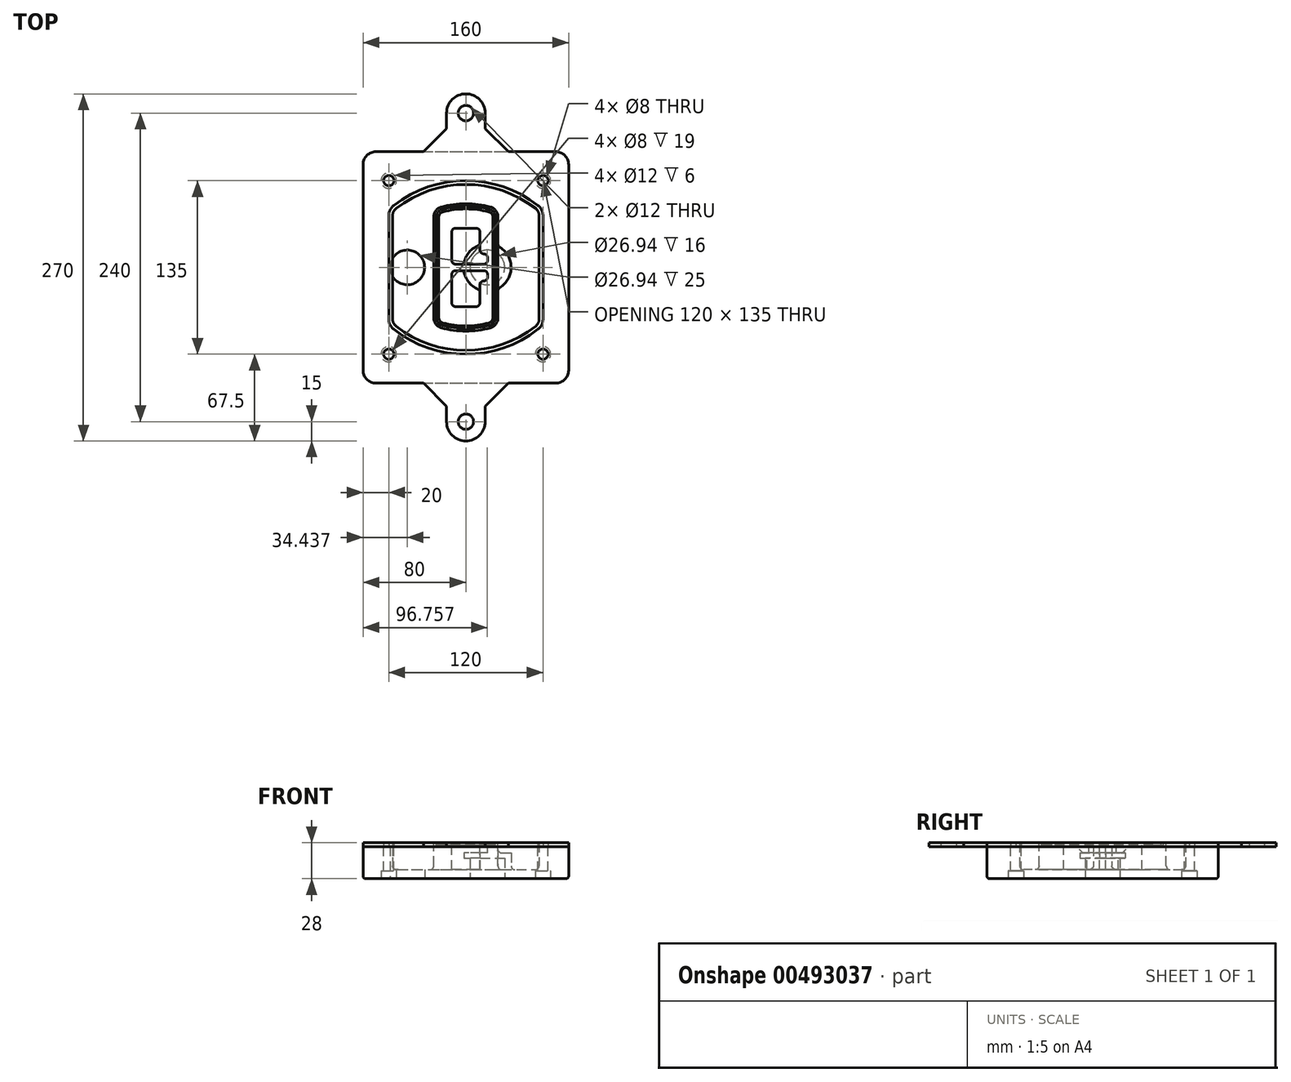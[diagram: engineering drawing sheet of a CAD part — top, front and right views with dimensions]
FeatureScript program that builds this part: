
annotation { "Feature Type Name" : "Feature", "Feature Type Description" : "" }
export const myFeature = defineFeature(function(context is Context, id is Id, definition is map)
    precondition{}
    {
        {
            var Q0;
            Q0=qCreatedBy(makeId("Top.planeOp"),FACE);
            var sketch = newSketch(context, id + "F0", { "sketchPlane" : qUnion([Q0])});
            skPoint(sketch, "E0.rect.middle", {"position": v(0, 0) * mm});
            skLineSegment(sketch, "E1.bottom", {"start": v(-70, -90) * mm, "end": v(70, -90) * mm});
            skLineSegment(sketch, "E1.top", {"start": v(-70, 90) * mm, "end": v(70, 90) * mm});
            skLineSegment(sketch, "E1.left", {"start": v(-80, -80) * mm, "end": v(-80, 80) * mm});
            skLineSegment(sketch, "E1.right", {"start": v(80, -80) * mm, "end": v(80, 80) * mm});
            skLineSegment(sketch, "E2", {"start": v(-80, 90) * mm, "end": v(80, -90) * mm, "construction": true});
            skLineSegment(sketch, "E3", {"start": v(80, 90) * mm, "end": v(-80, -90) * mm, "construction": true});
            skCircle(sketch, "E4", {"center": v(-60, 67.5) * mm, "radius": 4 * mm});
            skCircle(sketch, "E5", {"center": v(60, 67.5) * mm, "radius": 4 * mm});
            skCircle(sketch, "E6", {"center": v(60, -67.5) * mm, "radius": 4 * mm});
            skCircle(sketch, "E7", {"center": v(-60, -67.5) * mm, "radius": 4 * mm});
            skLineSegment(sketch, "E8", {"start": v(-60, 67.5) * mm, "end": v(60, 67.5) * mm, "construction": true});
            skLineSegment(sketch, "E9", {"start": v(60, 67.5) * mm, "end": v(60, -67.5) * mm, "construction": true});
            skLineSegment(sketch, "E10", {"start": v(60, -67.5) * mm, "end": v(-60, -67.5) * mm, "construction": true});
            skLineSegment(sketch, "E11", {"start": v(-60, -67.5) * mm, "end": v(-60, 67.5) * mm, "construction": true});
            skLineSegment(sketch, "E12", {"start": v(-60, 40.3) * mm, "end": v(-60, -40.3) * mm});
            skLineSegment(sketch, "E13", {"start": v(60, 40.3) * mm, "end": v(60, -40.3) * mm});
            skArc(sketch, "E14", {"start": v(56.15, 48.18) * mm, "mid": v(0, 67.5) * mm, "end": v(-56.15, 48.18) * mm});
            skArc(sketch, "E15", {"start": v(-56.15, -48.18) * mm, "mid": v(0, -67.5) * mm, "end": v(56.15, -48.18) * mm});
            skLineSegment(sketch, "E16", {"start": v(-60, 0) * mm, "end": v(60, 0) * mm, "construction": true});
            skPoint(sketch, "E17.visualSharp", {"position": v(-60, -45) * mm});
            skArc(sketch, "E17.filletArc", {"start": v(-60, -40.3) * mm, "mid": v(-58.99, -44.68) * mm, "end": v(-56.15, -48.18) * mm});
            skPoint(sketch, "E18.visualSharp", {"position": v(-60, 45) * mm});
            skArc(sketch, "E18.filletArc", {"start": v(-56.15, 48.18) * mm, "mid": v(-58.99, 44.68) * mm, "end": v(-60, 40.3) * mm});
            skPoint(sketch, "E19.visualSharp", {"position": v(60, 45) * mm});
            skArc(sketch, "E19.filletArc", {"start": v(60, 40.3) * mm, "mid": v(58.99, 44.68) * mm, "end": v(56.15, 48.18) * mm});
            skPoint(sketch, "E20.visualSharp", {"position": v(60, -45) * mm});
            skArc(sketch, "E20.filletArc", {"start": v(56.15, -48.18) * mm, "mid": v(58.99, -44.68) * mm, "end": v(60, -40.3) * mm});
            skPoint(sketch, "E21.visualSharp", {"position": v(-80, 90) * mm});
            skArc(sketch, "E21.filletArc", {"start": v(-70, 90) * mm, "mid": v(-77.07, 87.07) * mm, "end": v(-80, 80) * mm});
            skPoint(sketch, "E22.visualSharp", {"position": v(80, 90) * mm});
            skArc(sketch, "E22.filletArc", {"start": v(80, 80) * mm, "mid": v(77.07, 87.07) * mm, "end": v(70, 90) * mm});
            skPoint(sketch, "E23.visualSharp", {"position": v(80, -90) * mm});
            skArc(sketch, "E23.filletArc", {"start": v(70, -90) * mm, "mid": v(77.07, -87.07) * mm, "end": v(80, -80) * mm});
            skPoint(sketch, "E24.visualSharp", {"position": v(-80, -90) * mm});
            skArc(sketch, "E24.filletArc", {"start": v(-80, -80) * mm, "mid": v(-77.07, -87.07) * mm, "end": v(-70, -90) * mm});
            skArc(sketch, "E25.0", {"start": v(57, 40.3) * mm, "mid": v(56.3, 43.36) * mm, "end": v(54.3, 45.81) * mm});
            skLineSegment(sketch, "E25.1", {"start": v(57, 40.3) * mm, "end": v(57, -40.3) * mm});
            skArc(sketch, "E25.2", {"start": v(54.3, -45.81) * mm, "mid": v(56.3, -43.36) * mm, "end": v(57, -40.3) * mm});
            skArc(sketch, "E25.3", {"start": v(-54.3, -45.81) * mm, "mid": v(0, -64.5) * mm, "end": v(54.3, -45.81) * mm});
            skArc(sketch, "E25.4", {"start": v(-57, -40.3) * mm, "mid": v(-56.3, -43.36) * mm, "end": v(-54.3, -45.81) * mm});
            skArc(sketch, "E25.5", {"start": v(54.3, 45.81) * mm, "mid": v(0, 64.5) * mm, "end": v(-54.3, 45.81) * mm});
            skLineSegment(sketch, "E25.6", {"start": v(-57, 40.3) * mm, "end": v(-57, -40.3) * mm});
            skArc(sketch, "E25.7", {"start": v(-54.3, 45.81) * mm, "mid": v(-56.3, 43.36) * mm, "end": v(-57, 40.3) * mm});
            skArc(sketch, "E26.0", {"start": v(-58.62, 51.33) * mm, "mid": v(-62.58, 46.43) * mm, "end": v(-64, 40.3) * mm});
            skArc(sketch, "E26.1", {"start": v(58.62, 51.33) * mm, "mid": v(0, 71.5) * mm, "end": v(-58.62, 51.33) * mm});
            skArc(sketch, "E26.2", {"start": v(64, 40.3) * mm, "mid": v(62.58, 46.43) * mm, "end": v(58.62, 51.33) * mm});
            skLineSegment(sketch, "E26.3", {"start": v(64, 40.3) * mm, "end": v(64, -40.3) * mm});
            skArc(sketch, "E26.4", {"start": v(58.62, -51.33) * mm, "mid": v(62.58, -46.43) * mm, "end": v(64, -40.3) * mm});
            skLineSegment(sketch, "E26.5", {"start": v(-64, 40.3) * mm, "end": v(-64, -40.3) * mm});
            skArc(sketch, "E26.6", {"start": v(-58.62, -51.33) * mm, "mid": v(0, -71.5) * mm, "end": v(58.62, -51.33) * mm});
            skArc(sketch, "E26.7", {"start": v(-64, -40.3) * mm, "mid": v(-62.58, -46.43) * mm, "end": v(-58.62, -51.33) * mm});
            skSolve(sketch);
        }
        {
            var Q0;
            Q0=makeQuery(id+"F0.imprint","IMPRINT",FACE,{"disambiguationData":[TD([[makeQuery(id+"F0.imprint","IMPRINT",EDGE,{"derivedFrom":sQuery(id+"F0.wireOp",EDGE,"E1.bottom")}),1.0]])]});
            var Q1;
            Q1=makeQuery(id+"F0.imprint","IMPRINT",FACE,{"disambiguationData":[TD([[makeQuery(id+"F0.imprint","IMPRINT",EDGE,{"derivedFrom":sQuery(id+"F0.wireOp",EDGE,"E12")}),1.0]])]});
            var Q2;
            Q2=makeQuery(id+"F0.imprint","IMPRINT",FACE,{"disambiguationData":[TD([[makeQuery(id+"F0.imprint","IMPRINT",EDGE,{"derivedFrom":sQuery(id+"F0.wireOp",EDGE,"E25.0")}),1.0]])]});
            var Q3;
            Q3=makeQuery(id+"F0.imprint","IMPRINT",FACE,{"disambiguationData":[TD([[makeQuery(id+"F0.imprint","IMPRINT",EDGE,{"derivedFrom":sQuery(id+"F0.wireOp",EDGE,"E12")}),-1.0]])]});
            extrude(context, id + "F1", {"entities" : qUnion([Q0, Q1, Q2, Q3]), "oppositeDirection" : true, "depth" : 25 * mm});
        }
        {
            var Q0;
            Q0=makeQuery(id+"F0.imprint","IMPRINT",FACE,{"disambiguationData":[TD([[makeQuery(id+"F0.imprint","IMPRINT",EDGE,{"derivedFrom":sQuery(id+"F0.wireOp",EDGE,"E12")}),1.0]])]});
            extrude(context, id + "F2", {"entities" : qUnion([Q0]), "operationType" : NewBodyOperationType.ADD, "depth" : 3 * mm});
        }
        {
            var Q0;
            Q0=makeQuery(id+"F0.imprint","IMPRINT",FACE,{"disambiguationData":[TD([[makeQuery(id+"F0.imprint","IMPRINT",EDGE,{"derivedFrom":sQuery(id+"F0.wireOp",EDGE,"E25.0")}),1.0]])]});
            extrude(context, id + "F3", {"entities" : qUnion([Q0]), "operationType" : NewBodyOperationType.REMOVE, "oppositeDirection" : true, "depth" : 18 * mm});
        }
        {
            var Q0;
            Q0=makeQuery(id+"F2.opExtrude","CAP_FACE",FACE,{"disambiguationData":[OSD([sQuery(id+"F0.wireOp",EDGE,"E12"),sQuery(id+"F0.wireOp",EDGE,"E13"),sQuery(id+"F0.wireOp",EDGE,"E14"),sQuery(id+"F0.wireOp",EDGE,"E15"),sQuery(id+"F0.wireOp",EDGE,"E17.filletArc"),sQuery(id+"F0.wireOp",EDGE,"E18.filletArc"),sQuery(id+"F0.wireOp",EDGE,"E19.filletArc"),sQuery(id+"F0.wireOp",EDGE,"E20.filletArc"),sQuery(id+"F0.wireOp",EDGE,"E25.0"),sQuery(id+"F0.wireOp",EDGE,"E25.1"),sQuery(id+"F0.wireOp",EDGE,"E25.2"),sQuery(id+"F0.wireOp",EDGE,"E25.3"),sQuery(id+"F0.wireOp",EDGE,"E25.4"),sQuery(id+"F0.wireOp",EDGE,"E25.5"),sQuery(id+"F0.wireOp",EDGE,"E25.6"),sQuery(id+"F0.wireOp",EDGE,"E25.7")])],"isStart":false});
            var sketch = newSketch(context, id + "F4", { "sketchPlane" : qUnion([Q0])});
            skArc(sketch, "E27.0", {"start": v(-19.08, -46.97) * mm, "mid": v(0, -49.5) * mm, "end": v(19.08, -46.97) * mm});
            skArc(sketch, "E28.0", {"start": v(19.08, 46.97) * mm, "mid": v(0, 49.5) * mm, "end": v(-19.08, 46.97) * mm});
            skLineSegment(sketch, "E29", {"start": v(-25, 39.25) * mm, "end": v(-25, -39.25) * mm});
            skLineSegment(sketch, "E30", {"start": v(25, 39.25) * mm, "end": v(25, -39.25) * mm});
            skLineSegment(sketch, "E31", {"start": v(-25, 45.1) * mm, "end": v(25, 45.1) * mm, "construction": true});
            skLineSegment(sketch, "E32", {"start": v(-25, -45.1) * mm, "end": v(25, -45.1) * mm, "construction": true});
            skPoint(sketch, "E33.visualSharp", {"position": v(-25, 45.1) * mm});
            skArc(sketch, "E33.filletArc", {"start": v(-19.08, 46.97) * mm, "mid": v(-23.35, 44.11) * mm, "end": v(-25, 39.25) * mm});
            skPoint(sketch, "E34.visualSharp", {"position": v(25, 45.1) * mm});
            skArc(sketch, "E34.filletArc", {"start": v(25, 39.25) * mm, "mid": v(23.35, 44.11) * mm, "end": v(19.08, 46.97) * mm});
            skPoint(sketch, "E35.visualSharp", {"position": v(25, -45.1) * mm});
            skArc(sketch, "E35.filletArc", {"start": v(19.08, -46.97) * mm, "mid": v(23.35, -44.11) * mm, "end": v(25, -39.25) * mm});
            skPoint(sketch, "E36.visualSharp", {"position": v(-25, -45.1) * mm});
            skArc(sketch, "E36.filletArc", {"start": v(-25, -39.25) * mm, "mid": v(-23.35, -44.11) * mm, "end": v(-19.08, -46.97) * mm});
            skArc(sketch, "E37.0", {"start": v(54.3, 45.81) * mm, "mid": v(0, 64.5) * mm, "end": v(-54.3, 45.81) * mm});
            skArc(sketch, "E37.1", {"start": v(-54.3, 45.81) * mm, "mid": v(-56.3, 43.36) * mm, "end": v(-57, 40.3) * mm});
            skLineSegment(sketch, "E37.2", {"start": v(-57, 40.3) * mm, "end": v(-57, -40.3) * mm});
            skArc(sketch, "E37.3", {"start": v(-57, -40.3) * mm, "mid": v(-56.3, -43.36) * mm, "end": v(-54.3, -45.81) * mm});
            skArc(sketch, "E37.4", {"start": v(-54.3, -45.81) * mm, "mid": v(0, -64.5) * mm, "end": v(54.3, -45.81) * mm});
            skArc(sketch, "E37.5", {"start": v(54.3, -45.81) * mm, "mid": v(56.3, -43.36) * mm, "end": v(57, -40.3) * mm});
            skLineSegment(sketch, "E37.6", {"start": v(57, 40.3) * mm, "end": v(57, -40.3) * mm});
            skArc(sketch, "E37.7", {"start": v(57, 40.3) * mm, "mid": v(56.3, 43.36) * mm, "end": v(54.3, 45.81) * mm});
            skLineSegment(sketch, "E38.0", {"start": v(23, 39.25) * mm, "end": v(23, -39.25) * mm});
            skArc(sketch, "E38.1", {"start": v(18.56, -45.04) * mm, "mid": v(21.76, -42.9) * mm, "end": v(23, -39.25) * mm});
            skArc(sketch, "E38.2", {"start": v(-18.56, -45.04) * mm, "mid": v(0, -47.5) * mm, "end": v(18.56, -45.04) * mm});
            skArc(sketch, "E38.3", {"start": v(-23, -39.25) * mm, "mid": v(-21.76, -42.9) * mm, "end": v(-18.56, -45.04) * mm});
            skLineSegment(sketch, "E38.4", {"start": v(-23, 39.25) * mm, "end": v(-23, -39.25) * mm});
            skArc(sketch, "E38.5", {"start": v(23, 39.25) * mm, "mid": v(21.76, 42.9) * mm, "end": v(18.56, 45.04) * mm});
            skArc(sketch, "E38.6", {"start": v(-18.56, 45.04) * mm, "mid": v(-21.76, 42.9) * mm, "end": v(-23, 39.25) * mm});
            skArc(sketch, "E38.7", {"start": v(18.56, 45.04) * mm, "mid": v(0, 47.5) * mm, "end": v(-18.56, 45.04) * mm});
            skArc(sketch, "E39.0", {"start": v(21, 39.25) * mm, "mid": v(20.18, 41.68) * mm, "end": v(18.04, 43.1) * mm});
            skLineSegment(sketch, "E39.1", {"start": v(21, 39.25) * mm, "end": v(21, -39.25) * mm});
            skArc(sketch, "E39.2", {"start": v(18.04, -43.1) * mm, "mid": v(20.18, -41.68) * mm, "end": v(21, -39.25) * mm});
            skArc(sketch, "E39.3", {"start": v(-18.04, -43.1) * mm, "mid": v(0, -45.5) * mm, "end": v(18.04, -43.1) * mm});
            skArc(sketch, "E39.4", {"start": v(-21, -39.25) * mm, "mid": v(-20.18, -41.68) * mm, "end": v(-18.04, -43.1) * mm});
            skArc(sketch, "E39.5", {"start": v(18.04, 43.1) * mm, "mid": v(0, 45.5) * mm, "end": v(-18.04, 43.1) * mm});
            skLineSegment(sketch, "E39.6", {"start": v(-21, 39.25) * mm, "end": v(-21, -39.25) * mm});
            skArc(sketch, "E39.7", {"start": v(-18.04, 43.1) * mm, "mid": v(-20.18, 41.68) * mm, "end": v(-21, 39.25) * mm});
            skLineSegment(sketch, "E40", {"start": v(-25, 0) * mm, "end": v(25, 0) * mm, "construction": true});
            skLineSegment(sketch, "E41", {"start": v(-11, 5.5) * mm, "end": v(-11, 27.5) * mm});
            skLineSegment(sketch, "E42", {"start": v(-8, 30.5) * mm, "end": v(8, 30.5) * mm});
            skLineSegment(sketch, "E43", {"start": v(11, 27.5) * mm, "end": v(11, 13.5) * mm});
            skLineSegment(sketch, "E44", {"start": v(14, 10.5) * mm, "end": v(14, 10.5) * mm});
            skLineSegment(sketch, "E45", {"start": v(17, 7.5) * mm, "end": v(17, 5.5) * mm});
            skLineSegment(sketch, "E46", {"start": v(14, 2.5) * mm, "end": v(-8, 2.5) * mm});
            skPoint(sketch, "E47.visualSharp", {"position": v(-11, 30.5) * mm});
            skArc(sketch, "E47.filletArc", {"start": v(-8, 30.5) * mm, "mid": v(-10.12, 29.62) * mm, "end": v(-11, 27.5) * mm});
            skPoint(sketch, "E48.visualSharp", {"position": v(11, 30.5) * mm});
            skArc(sketch, "E48.filletArc", {"start": v(11, 27.5) * mm, "mid": v(10.12, 29.62) * mm, "end": v(8, 30.5) * mm});
            skPoint(sketch, "E49.visualSharp", {"position": v(11, 10.5) * mm});
            skArc(sketch, "E49.filletArc", {"start": v(11, 13.5) * mm, "mid": v(11.88, 11.38) * mm, "end": v(14, 10.5) * mm});
            skPoint(sketch, "E50.visualSharp", {"position": v(17, 10.5) * mm});
            skArc(sketch, "E50.filletArc", {"start": v(17, 7.5) * mm, "mid": v(16.12, 9.62) * mm, "end": v(14, 10.5) * mm});
            skPoint(sketch, "E51.visualSharp", {"position": v(17, 2.5) * mm});
            skArc(sketch, "E51.filletArc", {"start": v(14, 2.5) * mm, "mid": v(16.12, 3.38) * mm, "end": v(17, 5.5) * mm});
            skPoint(sketch, "E52.visualSharp", {"position": v(-11, 2.5) * mm});
            skArc(sketch, "E52.filletArc", {"start": v(-11, 5.5) * mm, "mid": v(-10.12, 3.38) * mm, "end": v(-8, 2.5) * mm});
            skLineSegment(sketch, "E53.0.MirrorCS", {"start": v(14, -2.5) * mm, "end": v(-8, -2.5) * mm});
            skArc(sketch, "E54.0.MirrorCS", {"start": v(-11, -5.5) * mm, "mid": v(-10.12, -3.38) * mm, "end": v(-8, -2.5) * mm});
            skLineSegment(sketch, "E55.0.MirrorCS", {"start": v(-11, -5.5) * mm, "end": v(-11, -27.5) * mm});
            skArc(sketch, "E56.0.MirrorCS", {"start": v(-8, -30.5) * mm, "mid": v(-10.12, -29.62) * mm, "end": v(-11, -27.5) * mm});
            skLineSegment(sketch, "E57.0.MirrorCS", {"start": v(-8, -30.5) * mm, "end": v(8, -30.5) * mm});
            skArc(sketch, "E58.0.MirrorCS", {"start": v(11, -27.5) * mm, "mid": v(10.12, -29.62) * mm, "end": v(8, -30.5) * mm});
            skLineSegment(sketch, "E59.0.MirrorCS", {"start": v(11, -27.5) * mm, "end": v(11, -13.5) * mm});
            skArc(sketch, "E60.0.MirrorCS", {"start": v(11, -13.5) * mm, "mid": v(11.88, -11.38) * mm, "end": v(14, -10.5) * mm});
            skArc(sketch, "E61.0.MirrorCS", {"start": v(17, -7.5) * mm, "mid": v(16.12, -9.62) * mm, "end": v(14, -10.5) * mm});
            skLineSegment(sketch, "E62.0.MirrorCS", {"start": v(17, -7.5) * mm, "end": v(17, -5.5) * mm});
            skArc(sketch, "E63.0.MirrorCS", {"start": v(14, -2.5) * mm, "mid": v(16.12, -3.38) * mm, "end": v(17, -5.5) * mm});
            skSolve(sketch);
        }
        {
            var Q0;
            Q0=makeQuery(id+"F4.imprint","IMPRINT",FACE,{"disambiguationData":[TD([[makeQuery(id+"F4.imprint","IMPRINT",EDGE,{"derivedFrom":sQuery(id+"F4.wireOp",EDGE,"E27.0")}),1.0]])]});
            var Q1;
            Q1=makeQuery(id+"F4.imprint","IMPRINT",FACE,{"disambiguationData":[TD([[makeQuery(id+"F4.imprint","IMPRINT",EDGE,{"derivedFrom":sQuery(id+"F4.wireOp",EDGE,"E38.0")}),-1.0]])]});
            var Q2;
            Q2=makeQuery(id+"F4.imprint","IMPRINT",FACE,{"disambiguationData":[TD([[makeQuery(id+"F4.imprint","IMPRINT",EDGE,{"derivedFrom":sQuery(id+"F4.wireOp",EDGE,"E39.0")}),1.0]])]});
            extrude(context, id + "F5", {"entities" : qUnion([Q0, Q1, Q2]), "operationType" : NewBodyOperationType.ADD, "endBound" : BoundingType.UP_TO_NEXT, "oppositeDirection" : true, "depth" : 25 * mm});
        }
        {
            var Q0;
            Q0=makeQuery(id+"F4.imprint","IMPRINT",FACE,{"disambiguationData":[TD([[makeQuery(id+"F4.imprint","IMPRINT",EDGE,{"derivedFrom":sQuery(id+"F4.wireOp",EDGE,"E38.0")}),-1.0]])]});
            extrude(context, id + "F6", {"entities" : qUnion([Q0]), "operationType" : NewBodyOperationType.REMOVE, "oppositeDirection" : true, "depth" : 2 * mm});
        }
        {
            var Q0;
            Q0=makeQuery(id+"F1.opExtrude","CAP_FACE",FACE,{"disambiguationData":[OSD([sQuery(id+"F0.wireOp",EDGE,"E1.bottom"),sQuery(id+"F0.wireOp",EDGE,"E1.top"),sQuery(id+"F0.wireOp",EDGE,"E1.left"),sQuery(id+"F0.wireOp",EDGE,"E1.right"),sQuery(id+"F0.wireOp",EDGE,"E4"),sQuery(id+"F0.wireOp",EDGE,"E5"),sQuery(id+"F0.wireOp",EDGE,"E6"),sQuery(id+"F0.wireOp",EDGE,"E7"),sQuery(id+"F0.wireOp",EDGE,"E21.filletArc"),sQuery(id+"F0.wireOp",EDGE,"E22.filletArc"),sQuery(id+"F0.wireOp",EDGE,"E23.filletArc"),sQuery(id+"F0.wireOp",EDGE,"E24.filletArc")])],"isStart":false});
            var sketch = newSketch(context, id + "F7", { "sketchPlane" : qUnion([Q0])});
            skCircle(sketch, "E64", {"center": v(16.76, 0) * mm, "radius": 13.47 * mm});
            skCircle(sketch, "E65", {"center": v(-45.56, 0) * mm, "radius": 13.47 * mm});
            skLineSegment(sketch, "E66", {"start": v(80, 0) * mm, "end": v(-80, 0) * mm});
            skCircle(sketch, "E67", {"center": v(16.76, 0) * mm, "radius": 18.47 * mm});
            skCircle(sketch, "E68", {"center": v(60, -67.5) * mm, "radius": 6 * mm});
            skCircle(sketch, "E69", {"center": v(-60, -67.5) * mm, "radius": 6 * mm});
            skCircle(sketch, "E70", {"center": v(-60, 67.5) * mm, "radius": 6 * mm});
            skCircle(sketch, "E71", {"center": v(60, 67.5) * mm, "radius": 6 * mm});
            skSolve(sketch);
        }
        {
            var Q0;
            {var subQ1=sQuery(id+"F7.wireOp",EDGE,"E66");var subQ4=sQuery(id+"F7.wireOp",EDGE,"E64");var subQ6=makeQuery(id+"F7.imprint","INTERSECT",VERTEX,{"disambiguationData":[OD(0.0)],"derivedFrom":[subQ4,subQ1]});Q0=makeQuery(id+"F7.imprint","IMPRINT",FACE,{"disambiguationData":[TD([[makeQuery(id+"F7.imprint","IMPRINT",EDGE,{"disambiguationData":[TD([[subQ6,-1.0]])],"derivedFrom":subQ4}),-1.0]])]});}
            var Q1;
            {var subQ0=sQuery(id+"F7.wireOp",EDGE,"E66");var subQ1=sQuery(id+"F7.wireOp",EDGE,"E64");var subQ3=makeQuery(id+"F7.imprint","INTERSECT",VERTEX,{"disambiguationData":[OD(0.0)],"derivedFrom":[subQ1,subQ0]});Q1=makeQuery(id+"F7.imprint","IMPRINT",FACE,{"disambiguationData":[TD([[makeQuery(id+"F7.imprint","IMPRINT",EDGE,{"disambiguationData":[TD([[subQ3,-1.0]])],"derivedFrom":subQ1}),1.0]])]});}
            var Q2;
            {var subQ0=sQuery(id+"F7.wireOp",EDGE,"E66");var subQ1=sQuery(id+"F7.wireOp",EDGE,"E64");var subQ3=makeQuery(id+"F7.imprint","INTERSECT",VERTEX,{"disambiguationData":[OD(0.0)],"derivedFrom":[subQ1,subQ0]});Q2=makeQuery(id+"F7.imprint","IMPRINT",FACE,{"disambiguationData":[TD([[makeQuery(id+"F7.imprint","IMPRINT",EDGE,{"disambiguationData":[TD([[subQ3,1.0]])],"derivedFrom":subQ1}),1.0]])]});}
            var Q3;
            {var subQ1=sQuery(id+"F7.wireOp",EDGE,"E66");var subQ4=sQuery(id+"F7.wireOp",EDGE,"E64");var subQ6=makeQuery(id+"F7.imprint","INTERSECT",VERTEX,{"disambiguationData":[OD(0.0)],"derivedFrom":[subQ4,subQ1]});Q3=makeQuery(id+"F7.imprint","IMPRINT",FACE,{"disambiguationData":[TD([[makeQuery(id+"F7.imprint","IMPRINT",EDGE,{"disambiguationData":[TD([[subQ6,1.0]])],"derivedFrom":subQ4}),-1.0]])]});}
            extrude(context, id + "F8", {"entities" : qUnion([Q0, Q1, Q2, Q3]), "operationType" : NewBodyOperationType.ADD, "oppositeDirection" : true, "depth" : 20 * mm});
        }
        {
            var Q0;
            {var subQ0=sQuery(id+"F7.wireOp",EDGE,"E66");var subQ1=sQuery(id+"F7.wireOp",EDGE,"E64");var subQ3=makeQuery(id+"F7.imprint","INTERSECT",VERTEX,{"disambiguationData":[OD(0.0)],"derivedFrom":[subQ1,subQ0]});Q0=makeQuery(id+"F7.imprint","IMPRINT",FACE,{"disambiguationData":[TD([[makeQuery(id+"F7.imprint","IMPRINT",EDGE,{"disambiguationData":[TD([[subQ3,-1.0]])],"derivedFrom":subQ1}),1.0]])]});}
            var Q1;
            {var subQ0=sQuery(id+"F7.wireOp",EDGE,"E66");var subQ1=sQuery(id+"F7.wireOp",EDGE,"E64");var subQ3=makeQuery(id+"F7.imprint","INTERSECT",VERTEX,{"disambiguationData":[OD(0.0)],"derivedFrom":[subQ1,subQ0]});Q1=makeQuery(id+"F7.imprint","IMPRINT",FACE,{"disambiguationData":[TD([[makeQuery(id+"F7.imprint","IMPRINT",EDGE,{"disambiguationData":[TD([[subQ3,1.0]])],"derivedFrom":subQ1}),1.0]])]});}
            extrude(context, id + "F9", {"entities" : qUnion([Q0, Q1]), "operationType" : NewBodyOperationType.REMOVE, "oppositeDirection" : true, "depth" : 16 * mm});
        }
        {
            var Q0;
            {var subQ0=sQuery(id+"F7.wireOp",EDGE,"E66");var subQ1=sQuery(id+"F7.wireOp",EDGE,"E65");var subQ3=makeQuery(id+"F7.imprint","INTERSECT",VERTEX,{"disambiguationData":[OD(0.0)],"derivedFrom":[subQ1,subQ0]});Q0=makeQuery(id+"F7.imprint","IMPRINT",FACE,{"disambiguationData":[TD([[makeQuery(id+"F7.imprint","IMPRINT",EDGE,{"disambiguationData":[TD([[subQ3,-1.0]])],"derivedFrom":subQ1}),1.0]])]});}
            var Q1;
            {var subQ0=sQuery(id+"F7.wireOp",EDGE,"E66");var subQ1=sQuery(id+"F7.wireOp",EDGE,"E65");var subQ3=makeQuery(id+"F7.imprint","INTERSECT",VERTEX,{"disambiguationData":[OD(0.0)],"derivedFrom":[subQ1,subQ0]});Q1=makeQuery(id+"F7.imprint","IMPRINT",FACE,{"disambiguationData":[TD([[makeQuery(id+"F7.imprint","IMPRINT",EDGE,{"disambiguationData":[TD([[subQ3,1.0]])],"derivedFrom":subQ1}),1.0]])]});}
            extrude(context, id + "F10", {"entities" : qUnion([Q0, Q1]), "operationType" : NewBodyOperationType.REMOVE, "oppositeDirection" : true, "depth" : 25 * mm});
        }
        {
            var Q0;
            Q0=makeQuery(id+"F7.imprint","IMPRINT",FACE,{"disambiguationData":[TD([[makeQuery(id+"F7.imprint","IMPRINT",EDGE,{"derivedFrom":sQuery(id+"F7.wireOp",EDGE,"E68")}),1.0]])]});
            var Q1;
            Q1=makeQuery(id+"F7.imprint","IMPRINT",FACE,{"disambiguationData":[TD([[makeQuery(id+"F7.imprint","IMPRINT",EDGE,{"derivedFrom":makeQuery(id+"F1.opExtrude","CAP_EDGE",EDGE,{"disambiguationData":[OSD([sQuery(id+"F0.wireOp",EDGE,"E5")])],"isStart":false})}),-1.0]])]});
            var Q2;
            Q2=makeQuery(id+"F7.imprint","IMPRINT",FACE,{"disambiguationData":[TD([[makeQuery(id+"F7.imprint","IMPRINT",EDGE,{"derivedFrom":sQuery(id+"F7.wireOp",EDGE,"E69")}),1.0]])]});
            var Q3;
            Q3=makeQuery(id+"F7.imprint","IMPRINT",FACE,{"disambiguationData":[TD([[makeQuery(id+"F7.imprint","IMPRINT",EDGE,{"derivedFrom":makeQuery(id+"F1.opExtrude","CAP_EDGE",EDGE,{"disambiguationData":[OSD([sQuery(id+"F0.wireOp",EDGE,"E4")])],"isStart":false})}),-1.0]])]});
            var Q4;
            Q4=makeQuery(id+"F7.imprint","IMPRINT",FACE,{"disambiguationData":[TD([[makeQuery(id+"F7.imprint","IMPRINT",EDGE,{"derivedFrom":sQuery(id+"F7.wireOp",EDGE,"E70")}),1.0]])]});
            var Q5;
            Q5=makeQuery(id+"F7.imprint","IMPRINT",FACE,{"disambiguationData":[TD([[makeQuery(id+"F7.imprint","IMPRINT",EDGE,{"derivedFrom":makeQuery(id+"F1.opExtrude","CAP_EDGE",EDGE,{"disambiguationData":[OSD([sQuery(id+"F0.wireOp",EDGE,"E7")])],"isStart":false})}),-1.0]])]});
            var Q6;
            Q6=makeQuery(id+"F7.imprint","IMPRINT",FACE,{"disambiguationData":[TD([[makeQuery(id+"F7.imprint","IMPRINT",EDGE,{"derivedFrom":sQuery(id+"F7.wireOp",EDGE,"E71")}),1.0]])]});
            var Q7;
            Q7=makeQuery(id+"F7.imprint","IMPRINT",FACE,{"disambiguationData":[TD([[makeQuery(id+"F7.imprint","IMPRINT",EDGE,{"derivedFrom":makeQuery(id+"F1.opExtrude","CAP_EDGE",EDGE,{"disambiguationData":[OSD([sQuery(id+"F0.wireOp",EDGE,"E6")])],"isStart":false})}),-1.0]])]});
            extrude(context, id + "F11", {"entities" : qUnion([Q0, Q1, Q2, Q3, Q4, Q5, Q6, Q7]), "operationType" : NewBodyOperationType.REMOVE, "oppositeDirection" : true, "depth" : 6 * mm});
        }
        {
            var Q0;
            Q0=makeQuery(id+"F9.boolean.opBoolean","COPY",FACE,{"derivedFrom":makeQuery(id+"F9.opExtrude","CAP_FACE",FACE,{"disambiguationData":[OSD([sQuery(id+"F7.wireOp",EDGE,"E64")])],"isStart":false})});
            var sketch = newSketch(context, id + "F12", { "sketchPlane" : qUnion([Q0])});
            skArc(sketch, "E72.0", {"start": v(11, 17.55) * mm, "mid": v(2.57, 11.82) * mm, "end": v(-1.54, 2.5) * mm});
            skArc(sketch, "E72.1", {"start": v(-1.54, -2.5) * mm, "mid": v(2.57, -11.82) * mm, "end": v(11, -17.55) * mm});
            skLineSegment(sketch, "E73", {"start": v(-1.54, -2.5) * mm, "end": v(14, -2.5) * mm});
            skLineSegment(sketch, "E74.0", {"start": v(14, 2.5) * mm, "end": v(-1.54, 2.5) * mm});
            skArc(sketch, "E74.1", {"start": v(14, 2.5) * mm, "mid": v(16.12, 3.38) * mm, "end": v(17, 5.5) * mm});
            skLineSegment(sketch, "E74.2", {"start": v(17, 7.5) * mm, "end": v(17, 5.5) * mm});
            skArc(sketch, "E74.3", {"start": v(17, 7.5) * mm, "mid": v(16.12, 9.62) * mm, "end": v(14, 10.5) * mm});
            skArc(sketch, "E74.4", {"start": v(11, 13.5) * mm, "mid": v(11.88, 11.38) * mm, "end": v(14, 10.5) * mm});
            skLineSegment(sketch, "E74.5", {"start": v(11, 17.55) * mm, "end": v(11, 13.5) * mm});
            skLineSegment(sketch, "E74.7", {"start": v(14, -2.5) * mm, "end": v(-1.54, -2.5) * mm});
            skArc(sketch, "E74.8", {"start": v(14, -2.5) * mm, "mid": v(16.12, -3.38) * mm, "end": v(17, -5.5) * mm});
            skLineSegment(sketch, "E74.9", {"start": v(17, -7.5) * mm, "end": v(17, -5.5) * mm});
            skArc(sketch, "E74.10", {"start": v(17, -7.5) * mm, "mid": v(16.12, -9.62) * mm, "end": v(14, -10.5) * mm});
            skArc(sketch, "E74.11", {"start": v(11, -13.5) * mm, "mid": v(11.88, -11.38) * mm, "end": v(14, -10.5) * mm});
            skLineSegment(sketch, "E74.12", {"start": v(11, -17.55) * mm, "end": v(11, -13.5) * mm});
            skPoint(sketch, "E75.orphan", {"position": v(11, -27.5) * mm});
            skPoint(sketch, "E76.orphan", {"position": v(-8, -2.5) * mm});
            skPoint(sketch, "E77.orphan", {"position": v(-8, 2.5) * mm});
            skPoint(sketch, "E78.orphan", {"position": v(11, 27.5) * mm});
            skSolve(sketch);
        }
        {
            var Q0;
            {var subQ7=sQuery(id+"F12.wireOp",EDGE,"E72.0");var subQ14=sQuery(id+"F12.wireOp",EDGE,"E72.1");var subQ16=sQuery(id+"F12.wireOp",EDGE,"E74.1");var subQ18=sQuery(id+"F12.wireOp",EDGE,"E74.8");Q0=qUnion([makeQuery(id+"F12.imprint","IMPRINT",FACE,{"disambiguationData":[TD([[makeQuery(id+"F12.imprint","IMPRINT",EDGE,{"derivedFrom":subQ7}),1.0]])]}),makeQuery(id+"F12.imprint","IMPRINT",FACE,{"disambiguationData":[TD([[makeQuery(id+"F12.imprint","IMPRINT",EDGE,{"derivedFrom":subQ14}),1.0]])]}),makeQuery(id+"F12.imprint","IMPRINT",FACE,{"disambiguationData":[TD([[makeQuery(id+"F12.imprint","IMPRINT",EDGE,{"derivedFrom":subQ16}),1.0]])]}),makeQuery(id+"F12.imprint","IMPRINT",FACE,{"disambiguationData":[TD([[makeQuery(id+"F12.imprint","IMPRINT",EDGE,{"derivedFrom":subQ18}),-1.0]])]})]);}
            var Q1;
            Q1=makeQuery(id+"F5.boolean.opBoolean","SPLIT",FACE,{"disambiguationData":[TD([makeQuery(id+"F5.opExtrude","SWEPT_FACE",FACE,{"disambiguationData":[OSD([sQuery(id+"F4.wireOp",EDGE,"E41")])]})])],"derivedFrom":makeQuery(id+"F3.boolean.opBoolean","COPY",FACE,{"derivedFrom":makeQuery(id+"F3.opExtrude","CAP_FACE",FACE,{"disambiguationData":[OSD([sQuery(id+"F0.wireOp",EDGE,"E25.0"),sQuery(id+"F0.wireOp",EDGE,"E25.1"),sQuery(id+"F0.wireOp",EDGE,"E25.2"),sQuery(id+"F0.wireOp",EDGE,"E25.3"),sQuery(id+"F0.wireOp",EDGE,"E25.4"),sQuery(id+"F0.wireOp",EDGE,"E25.5"),sQuery(id+"F0.wireOp",EDGE,"E25.6"),sQuery(id+"F0.wireOp",EDGE,"E25.7")])],"isStart":false})})});
            extrude(context, id + "F13", {"entities" : qUnion([Q0]), "operationType" : NewBodyOperationType.REMOVE, "endBound" : BoundingType.UP_TO_SURFACE, "endBoundEntityFace" : qUnion([Q1]), "depth" : 25 * mm});
        }
        {
            var Q0;
            Q0=makeQuery(id+"F3.boolean.opBoolean","COPY",EDGE,{"derivedFrom":makeQuery(id+"F3.opExtrude","CAP_EDGE",EDGE,{"disambiguationData":[OSD([sQuery(id+"F0.wireOp",EDGE,"E25.6")])],"isStart":false})});
            var Q1;
            Q1=makeQuery(id+"F8.boolean.opBoolean","INTERSECT",EDGE,{"derivedFrom":[makeQuery(id+"F5.opExtrude","SWEPT_FACE",FACE,{"disambiguationData":[OSD([sQuery(id+"F4.wireOp",EDGE,"E30")])]}),makeQuery(id+"F8.opExtrude","CAP_FACE",FACE,{"disambiguationData":[OSD([sQuery(id+"F7.wireOp",EDGE,"E67")])],"isStart":false})]});
            var Q2;
            Q2=makeQuery(id+"F8.boolean.opBoolean","INTERSECT",EDGE,{"disambiguationData":[OD(1.0)],"derivedFrom":[makeQuery(id+"F5.opExtrude","SWEPT_FACE",FACE,{"disambiguationData":[OSD([sQuery(id+"F4.wireOp",EDGE,"E30")])]}),makeQuery(id+"F8.opExtrude","SWEPT_FACE",FACE,{"disambiguationData":[OSD([sQuery(id+"F7.wireOp",EDGE,"E67")])]})]});
            var Q3;
            {var subQ0=sQuery(id+"F4.wireOp",EDGE,"E30");Q3=makeQuery(id+"F8.boolean.opBoolean","SPLIT",EDGE,{"disambiguationData":[TD([makeQuery(id+"F5.opExtrude","SWEPT_FACE",FACE,{"disambiguationData":[OSD([sQuery(id+"F4.wireOp",EDGE,"E35.filletArc")])]})])],"derivedFrom":makeQuery(id+"F5.opExtrude","CAP_EDGE",EDGE,{"disambiguationData":[OSD([subQ0])],"isStart":false})});}
            var Q4;
            {var subQ0=sQuery(id+"F0.wireOp",EDGE,"E25.7");var subQ1=sQuery(id+"F0.wireOp",EDGE,"E25.1");var subQ2=sQuery(id+"F0.wireOp",EDGE,"E25.6");var subQ3=sQuery(id+"F0.wireOp",EDGE,"E25.5");var subQ4=sQuery(id+"F0.wireOp",EDGE,"E25.4");var subQ5=sQuery(id+"F0.wireOp",EDGE,"E25.0");var subQ6=sQuery(id+"F0.wireOp",EDGE,"E25.2");var subQ7=sQuery(id+"F0.wireOp",EDGE,"E25.3");Q4=makeQuery(id+"F8.boolean.opBoolean","INTERSECT",EDGE,{"derivedFrom":[makeQuery(id+"F5.boolean.opBoolean","SPLIT",FACE,{"disambiguationData":[TD([makeQuery(id+"F2.opExtrude","SWEPT_FACE",FACE,{"disambiguationData":[OSD([subQ5])]})])],"derivedFrom":makeQuery(id+"F3.boolean.opBoolean","COPY",FACE,{"derivedFrom":makeQuery(id+"F3.opExtrude","CAP_FACE",FACE,{"disambiguationData":[OSD([subQ5,subQ1,subQ6,subQ7,subQ4,subQ3,subQ2,subQ0])],"isStart":false})})}),makeQuery(id+"F8.opExtrude","SWEPT_FACE",FACE,{"disambiguationData":[OSD([sQuery(id+"F7.wireOp",EDGE,"E67")])]})]});}
            var Q5;
            Q5=makeQuery(id+"F8.boolean.opBoolean","INTERSECT",EDGE,{"disambiguationData":[OD(0.0)],"derivedFrom":[makeQuery(id+"F5.opExtrude","SWEPT_FACE",FACE,{"disambiguationData":[OSD([sQuery(id+"F4.wireOp",EDGE,"E30")])]}),makeQuery(id+"F8.opExtrude","SWEPT_FACE",FACE,{"disambiguationData":[OSD([sQuery(id+"F7.wireOp",EDGE,"E67")])]})]});
            fillet(context, id + "F14", {"entities" : qUnion([Q0, Q1, Q2, Q3, Q4, Q5]), "radius" : 3 * mm, "tangentPropagation" : true, "allowEdgeOverflow" : false});
        }
        {
            var Q0;
            Q0=makeQuery(id+"F1.opExtrude","CAP_EDGE",EDGE,{"disambiguationData":[OSD([sQuery(id+"F0.wireOp",EDGE,"E1.bottom")])],"isStart":false});
            fillet(context, id + "F15", {"entities" : qUnion([Q0]), "radius" : 2 * mm, "tangentPropagation" : true, "allowEdgeOverflow" : false});
        }
        {
            var Q0;
            {var subQ0=sQuery(id+"F0.wireOp",EDGE,"E21.filletArc");var subQ1=sQuery(id+"F0.wireOp",EDGE,"E7");var subQ2=sQuery(id+"F0.wireOp",EDGE,"E6");var subQ3=sQuery(id+"F0.wireOp",EDGE,"E5");var subQ4=sQuery(id+"F0.wireOp",EDGE,"E4");var subQ5=sQuery(id+"F0.wireOp",EDGE,"E22.filletArc");var subQ6=sQuery(id+"F0.wireOp",EDGE,"E1.bottom");var subQ7=sQuery(id+"F0.wireOp",EDGE,"E1.right");var subQ8=sQuery(id+"F0.wireOp",EDGE,"E1.top");var subQ9=sQuery(id+"F0.wireOp",EDGE,"E1.left");var subQ10=sQuery(id+"F0.wireOp",EDGE,"E23.filletArc");var subQ11=sQuery(id+"F0.wireOp",EDGE,"E24.filletArc");Q0=makeQuery(id+"F2.boolean.opBoolean","SPLIT",FACE,{"disambiguationData":[TD([makeQuery(id+"F1.opExtrude","SWEPT_FACE",FACE,{"disambiguationData":[OSD([subQ6])]})])],"derivedFrom":makeQuery(id+"F1.opExtrude","CAP_FACE",FACE,{"disambiguationData":[OSD([subQ6,subQ8,subQ9,subQ7,subQ4,subQ3,subQ2,subQ1,subQ0,subQ5,subQ10,subQ11])],"isStart":true})});}
            var sketch = newSketch(context, id + "F16", { "sketchPlane" : qUnion([Q0])});
            skLineSegment(sketch, "E79", {"start": v(0, 90) * mm, "end": v(0, 120) * mm, "construction": true});
            skCircle(sketch, "E80", {"center": v(0, 120) * mm, "radius": 6 * mm});
            skLineSegment(sketch, "E81", {"start": v(15, 120) * mm, "end": v(15, 108) * mm});
            skLineSegment(sketch, "E82", {"start": v(15, 108) * mm, "end": v(33, 90) * mm});
            skLineSegment(sketch, "E83", {"start": v(0, 90) * mm, "end": v(33, 90) * mm});
            skLineSegment(sketch, "E84.MirrorCS", {"start": v(0, 90) * mm, "end": v(-33, 90) * mm});
            skLineSegment(sketch, "E85.MirrorCS", {"start": v(-15, 120) * mm, "end": v(-15, 108) * mm});
            skLineSegment(sketch, "E86.MirrorCS", {"start": v(-15, 108) * mm, "end": v(-33, 90) * mm});
            skArc(sketch, "E87", {"start": v(-15, 120) * mm, "mid": v(0, 135) * mm, "end": v(15, 120) * mm});
            skLineSegment(sketch, "E88", {"start": v(-80, 0) * mm, "end": v(80, 0) * mm, "construction": true});
            skLineSegment(sketch, "E89.0", {"start": v(-70, 90) * mm, "end": v(70, 90) * mm});
            skArc(sketch, "E90.0", {"start": v(-70, 90) * mm, "mid": v(-77.07, 87.07) * mm, "end": v(-80, 80) * mm});
            skLineSegment(sketch, "E91.0", {"start": v(-80, -80) * mm, "end": v(-80, 80) * mm});
            skArc(sketch, "E92.0", {"start": v(-80, -80) * mm, "mid": v(-77.07, -87.07) * mm, "end": v(-70, -90) * mm});
            skLineSegment(sketch, "E93.0", {"start": v(-70, -90) * mm, "end": v(70, -90) * mm});
            skArc(sketch, "E94.0", {"start": v(70, -90) * mm, "mid": v(77.07, -87.07) * mm, "end": v(80, -80) * mm});
            skLineSegment(sketch, "E95.0", {"start": v(80, -80) * mm, "end": v(80, 80) * mm});
            skArc(sketch, "E96.0", {"start": v(80, 80) * mm, "mid": v(77.07, 87.07) * mm, "end": v(70, 90) * mm});
            skArc(sketch, "E97.0", {"start": v(56.15, 48.18) * mm, "mid": v(0, 67.5) * mm, "end": v(-56.15, 48.18) * mm});
            skLineSegment(sketch, "E98.0.0", {"start": v(70, 90) * mm, "end": v(-70, 90) * mm});
            skLineSegment(sketch, "E98.0.2", {"start": v(-80, 80) * mm, "end": v(-80, -80) * mm});
            skCircle(sketch, "E99.0", {"center": v(60, 67.5) * mm, "radius": 4 * mm});
            skCircle(sketch, "E100.0", {"center": v(-60, 67.5) * mm, "radius": 4 * mm});
            skCircle(sketch, "E101.0", {"center": v(60, -67.5) * mm, "radius": 4 * mm});
            skLineSegment(sketch, "E102.0", {"start": v(60, 40.3) * mm, "end": v(60, -40.3) * mm});
            skArc(sketch, "E103.0", {"start": v(-56.15, -48.18) * mm, "mid": v(0, -67.5) * mm, "end": v(56.15, -48.18) * mm});
            skArc(sketch, "E104.0", {"start": v(-60, -40.3) * mm, "mid": v(-58.99, -44.68) * mm, "end": v(-56.15, -48.18) * mm});
            skLineSegment(sketch, "E105.0", {"start": v(-60, 40.3) * mm, "end": v(-60, -40.3) * mm});
            skArc(sketch, "E106.0", {"start": v(-56.15, 48.18) * mm, "mid": v(-58.99, 44.68) * mm, "end": v(-60, 40.3) * mm});
            skLineSegment(sketch, "E107.MirrorCS", {"start": v(70, -90) * mm, "end": v(-70, -90) * mm});
            skArc(sketch, "E108.MirrorCS", {"start": v(-70, -90) * mm, "mid": v(-77.07, -87.07) * mm, "end": v(-80, -80) * mm});
            skArc(sketch, "E109.MirrorCS", {"start": v(80, -80) * mm, "mid": v(77.07, -87.07) * mm, "end": v(70, -90) * mm});
            skLineSegment(sketch, "E110.MirrorCS", {"start": v(0, -90) * mm, "end": v(-33, -90) * mm});
            skLineSegment(sketch, "E111.MirrorCS", {"start": v(0, -90) * mm, "end": v(33, -90) * mm});
            skLineSegment(sketch, "E112.MirrorCS", {"start": v(0, -90) * mm, "end": v(0, -120) * mm, "construction": true});
            skLineSegment(sketch, "E113.MirrorCS", {"start": v(-15, -108) * mm, "end": v(-33, -90) * mm});
            skArc(sketch, "E114.MirrorCS", {"start": v(-15, -120) * mm, "mid": v(0, -135) * mm, "end": v(15, -120) * mm});
            skArc(sketch, "E115.MirrorCS", {"start": v(56.15, -48.18) * mm, "mid": v(0, -67.5) * mm, "end": v(-56.15, -48.18) * mm});
            skArc(sketch, "E116.MirrorCS", {"start": v(-56.15, -48.18) * mm, "mid": v(-58.99, -44.68) * mm, "end": v(-60, -40.3) * mm});
            skLineSegment(sketch, "E117.MirrorCS", {"start": v(15, -120) * mm, "end": v(15, -108) * mm});
            skLineSegment(sketch, "E118.MirrorCS", {"start": v(-15, -120) * mm, "end": v(-15, -108) * mm});
            skLineSegment(sketch, "E119.MirrorCS", {"start": v(15, -108) * mm, "end": v(33, -90) * mm});
            skCircle(sketch, "E120.MirrorC", {"center": v(0, -120) * mm, "radius": 6 * mm});
            skCircle(sketch, "E121.MirrorC", {"center": v(-60, -67.5) * mm, "radius": 4 * mm});
            skArc(sketch, "E122.0", {"start": v(56.15, -48.18) * mm, "mid": v(58.99, -44.68) * mm, "end": v(60, -40.3) * mm});
            skPoint(sketch, "E123.0", {"position": v(57, 40.3) * mm});
            skArc(sketch, "E124.0", {"start": v(60, 40.3) * mm, "mid": v(58.99, 44.68) * mm, "end": v(56.15, 48.18) * mm});
            skSolve(sketch);
        }
        {
            var Q0;
            Q0 = qSketchRegion(id + "F16", true);
            var Q1;
            Q1=makeQuery(id+"F2.opExtrude","CAP_FACE",FACE,{"disambiguationData":[OSD([sQuery(id+"F0.wireOp",EDGE,"E12"),sQuery(id+"F0.wireOp",EDGE,"E13"),sQuery(id+"F0.wireOp",EDGE,"E14"),sQuery(id+"F0.wireOp",EDGE,"E15"),sQuery(id+"F0.wireOp",EDGE,"E17.filletArc"),sQuery(id+"F0.wireOp",EDGE,"E18.filletArc"),sQuery(id+"F0.wireOp",EDGE,"E19.filletArc"),sQuery(id+"F0.wireOp",EDGE,"E20.filletArc"),sQuery(id+"F0.wireOp",EDGE,"E25.0"),sQuery(id+"F0.wireOp",EDGE,"E25.1"),sQuery(id+"F0.wireOp",EDGE,"E25.2"),sQuery(id+"F0.wireOp",EDGE,"E25.3"),sQuery(id+"F0.wireOp",EDGE,"E25.4"),sQuery(id+"F0.wireOp",EDGE,"E25.5"),sQuery(id+"F0.wireOp",EDGE,"E25.6"),sQuery(id+"F0.wireOp",EDGE,"E25.7")])],"isStart":false});
            extrude(context, id + "F17", {"entities" : qUnion([Q0]), "endBound" : BoundingType.UP_TO_SURFACE, "endBoundEntityFace" : qUnion([Q1]), "depth" : 25 * mm});
        }
    });
